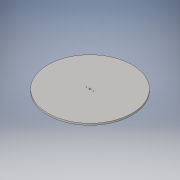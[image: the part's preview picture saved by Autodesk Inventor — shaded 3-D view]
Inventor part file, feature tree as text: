
AUTODESK INVENTOR PART (.ipt)
format: ipt  version: 2016 (Build 200138000, 138)  size: 115,200 bytes
history: native  units: in
note: dims shown in document units (in); Inventor stores cm internally (conversion verified against a paired STEP export)
features: extrude x1, sketch x1
ambient origin geometry x8: Origin, YZ Plane, XZ Plane, XY Plane, X Axis, Y Axis, Z Axis, Center Point
bodies: Solid1 (feature_tree)
feature tree (2):
  extrude  "Extrusion1"  TaperAngle=45.0deg  [1 undecoded]
  sketch  "Sketch1"  dims[d0=9.0in d1=45.0deg d2=45.0deg d3=135.0deg d4=135.0deg d12=0.175in d13=0.375in d14=0.075in d15=0.375in d16=0.075in d17=0.18in d18=0.0in d22=67.5deg d23=22.5deg d24=22.5deg d25=22.5deg d26=22.5deg d27=7.0in d28=22.5deg d29=22.5deg d30=22.5deg]
note: 1 required parameter value undecoded (feature->parameter linkage not recoverable at this tier; creation-order binding heuristic only, values carry confidence <= 0.55)
